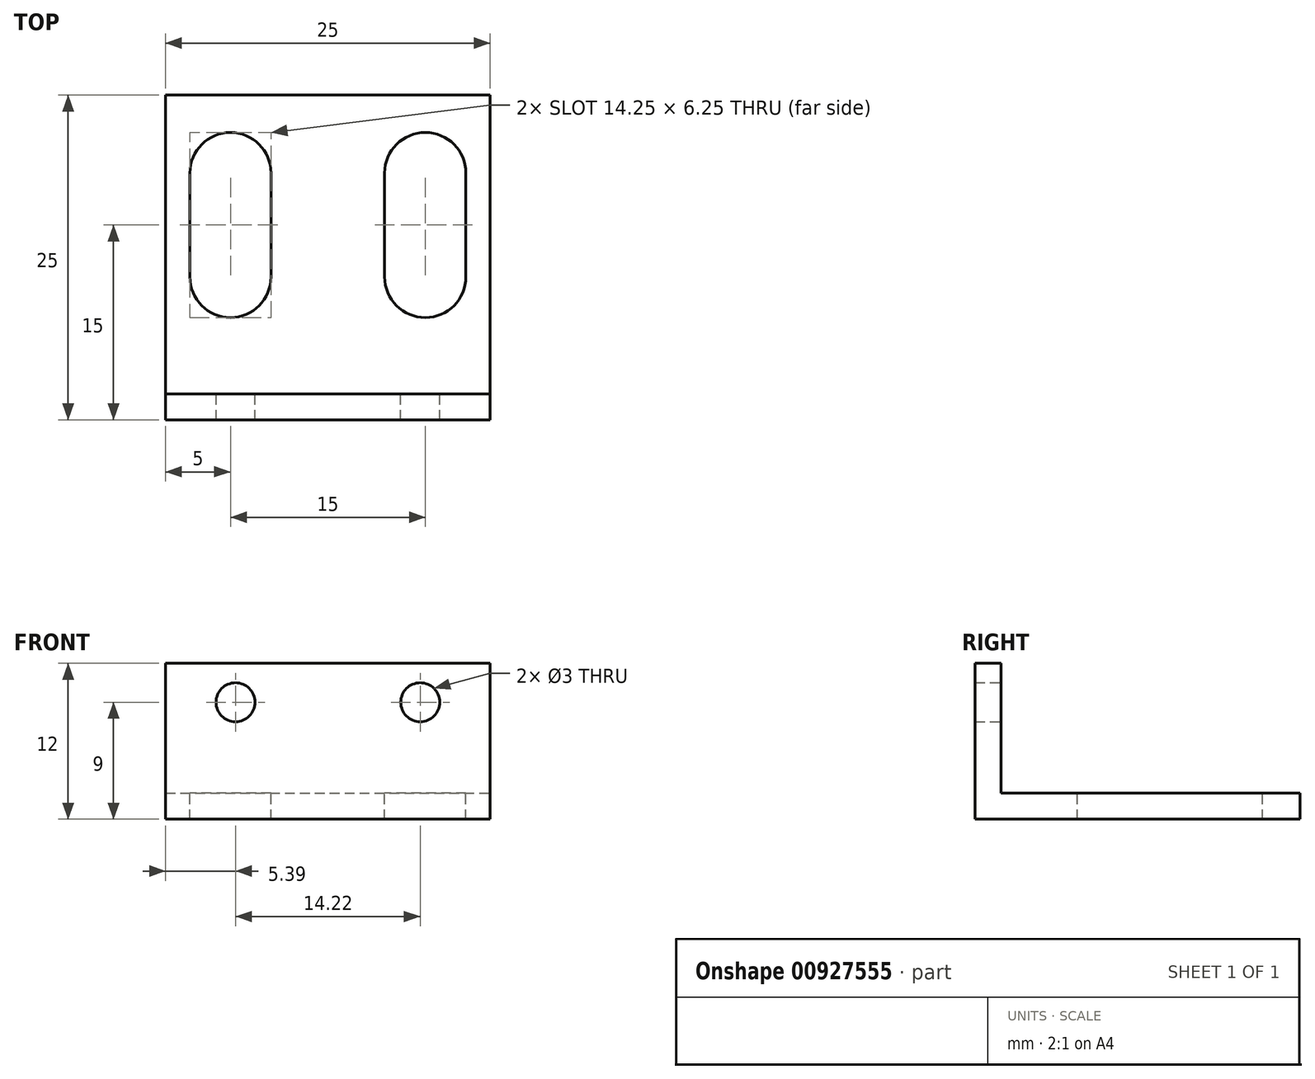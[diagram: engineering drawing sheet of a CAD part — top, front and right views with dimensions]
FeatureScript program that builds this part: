
annotation { "Feature Type Name" : "Feature", "Feature Type Description" : "" }
export const myFeature = defineFeature(function(context is Context, id is Id, definition is map)
    precondition{}
    {
        {
            var Q0;
            Q0=qCreatedBy(makeId("Right.planeOp"),FACE);
            var sketch = newSketch(context, id + "F0", { "sketchPlane" : qUnion([Q0])});
            skLineSegment(sketch, "E0", {"start": v(0, 0) * mm, "end": v(25, 0) * mm});
            skLineSegment(sketch, "E1", {"start": v(0, 0) * mm, "end": v(0, 12) * mm});
            skLineSegment(sketch, "E2.0", {"start": v(2, 2) * mm, "end": v(2, 12) * mm});
            skLineSegment(sketch, "E2.1", {"start": v(2, 2) * mm, "end": v(25, 2) * mm});
            skLineSegment(sketch, "E3", {"start": v(2, 12) * mm, "end": v(0, 12) * mm});
            skLineSegment(sketch, "E4", {"start": v(25, 2) * mm, "end": v(25, 0) * mm});
            skSolve(sketch);
        }
        {
            var Q0;
            Q0=makeQuery(id+"F0.imprint","IMPRINT",FACE,{"disambiguationData":[TD([[makeQuery(id+"F0.imprint","IMPRINT",EDGE,{"derivedFrom":sQuery(id+"F0.wireOp",EDGE,"E0")}),1.0]])]});
            extrude(context, id + "F1", {"entities" : qUnion([Q0]), "oppositeDirection" : true, "depth" : 25 * mm, "offsetDistance" : 25 * mm});
        }
        {
            var Q0;
            Q0=makeQuery(id+"F1.opExtrude","SWEPT_FACE",FACE,{"disambiguationData":[OSD([sQuery(id+"F0.wireOp",EDGE,"E2.0")])]});
            var sketch = newSketch(context, id + "F2", { "sketchPlane" : qUnion([Q0])});
            skCircle(sketch, "E5", {"center": v(5.39, 9) * mm, "radius": 1.5 * mm});
            skCircle(sketch, "E6", {"center": v(19.61, 9) * mm, "radius": 1.5 * mm});
            skSolve(sketch);
        }
        {
            var Q0;
            Q0 = qSketchRegion(id + "F2", true);
            extrude(context, id + "F3", {"entities" : qUnion([Q0]), "operationType" : NewBodyOperationType.REMOVE, "oppositeDirection" : true, "depth" : 25 * mm, "offsetDistance" : 25 * mm});
        }
        {
            var Q0;
            Q0=makeQuery(id+"F1.opExtrude","SWEPT_FACE",FACE,{"disambiguationData":[OSD([sQuery(id+"F0.wireOp",EDGE,"E2.1")])]});
            var sketch = newSketch(context, id + "F4", { "sketchPlane" : qUnion([Q0])});
            skArc(sketch, "E7", {"start": v(-16.88, 19) * mm, "mid": v(-20, 22.13) * mm, "end": v(-23.12, 19) * mm});
            skArc(sketch, "E8", {"start": v(-23.12, 11) * mm, "mid": v(-20, 7.88) * mm, "end": v(-16.88, 11) * mm});
            skArc(sketch, "E9", {"start": v(-1.88, 19) * mm, "mid": v(-5, 22.13) * mm, "end": v(-8.12, 19) * mm});
            skArc(sketch, "E10", {"start": v(-8.12, 11) * mm, "mid": v(-5, 7.88) * mm, "end": v(-1.88, 11) * mm});
            skLineSegment(sketch, "E11", {"start": v(-23.12, 19) * mm, "end": v(-23.12, 11) * mm});
            skLineSegment(sketch, "E12", {"start": v(-16.88, 19) * mm, "end": v(-16.88, 11) * mm});
            skLineSegment(sketch, "E13", {"start": v(-8.12, 19) * mm, "end": v(-8.12, 11) * mm});
            skLineSegment(sketch, "E14", {"start": v(-1.88, 19) * mm, "end": v(-1.87, 11) * mm});
            skSolve(sketch);
        }
        {
            var Q0;
            Q0 = qSketchRegion(id + "F4", true);
            extrude(context, id + "F5", {"entities" : qUnion([Q0]), "operationType" : NewBodyOperationType.REMOVE, "oppositeDirection" : true, "depth" : 25 * mm, "offsetDistance" : 25 * mm});
        }
    });
